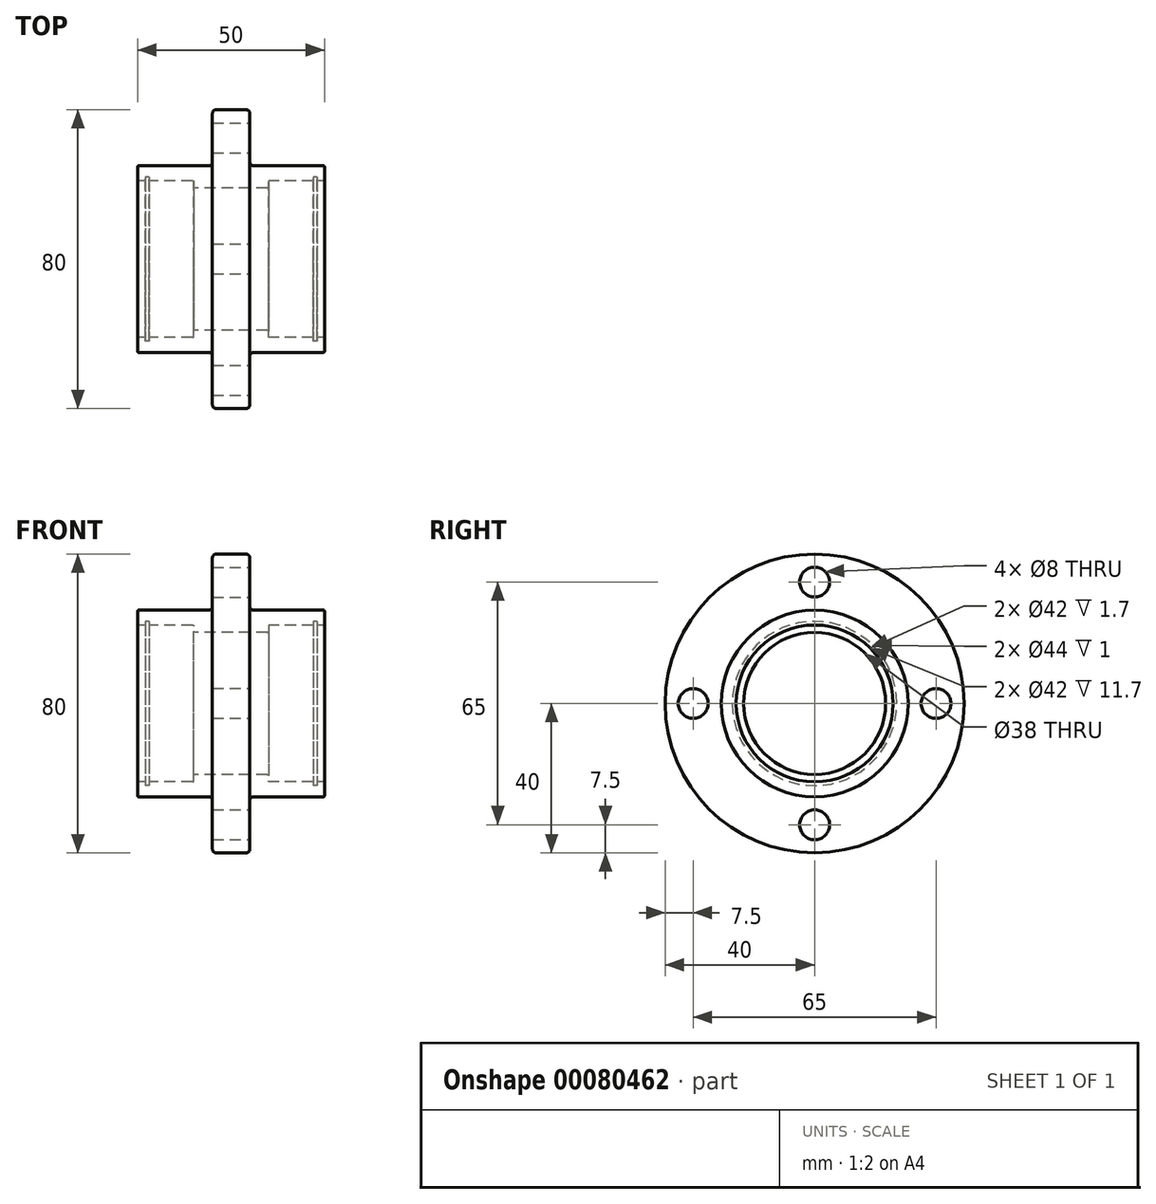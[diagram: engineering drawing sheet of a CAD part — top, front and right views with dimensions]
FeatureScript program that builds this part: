
annotation { "Feature Type Name" : "Feature", "Feature Type Description" : "" }
export const myFeature = defineFeature(function(context is Context, id is Id, definition is map)
    precondition{}
    {
        {
            var Q0;
            Q0=qCreatedBy(makeId("Front.planeOp"),FACE);
            var sketch = newSketch(context, id + "F0", { "sketchPlane" : qUnion([Q0])});
            skLineSegment(sketch, "E0", {"start": v(0, 0) * mm, "end": v(52.45, 0) * mm, "construction": true});
            skLineSegment(sketch, "E1", {"start": v(0, 21) * mm, "end": v(15, 21) * mm});
            skLineSegment(sketch, "E2", {"start": v(15, 21) * mm, "end": v(15, 19) * mm});
            skLineSegment(sketch, "E3", {"start": v(15, 19) * mm, "end": v(35, 19) * mm});
            skLineSegment(sketch, "E4", {"start": v(50, 21) * mm, "end": v(50, 25) * mm});
            skLineSegment(sketch, "E5", {"start": v(50, 25) * mm, "end": v(30, 25) * mm});
            skLineSegment(sketch, "E6", {"start": v(30, 25) * mm, "end": v(30, 40) * mm});
            skLineSegment(sketch, "E7", {"start": v(0, 25) * mm, "end": v(0, 21) * mm});
            skLineSegment(sketch, "E8.bottom", {"start": v(2, 21) * mm, "end": v(3, 21) * mm});
            skLineSegment(sketch, "E8.top", {"start": v(2, 22) * mm, "end": v(3, 22) * mm});
            skLineSegment(sketch, "E8.left", {"start": v(2, 21) * mm, "end": v(2, 22) * mm});
            skLineSegment(sketch, "E8.right", {"start": v(3, 21) * mm, "end": v(3, 22) * mm});
            skLineSegment(sketch, "E9", {"start": v(0, 25) * mm, "end": v(20, 25) * mm});
            skLineSegment(sketch, "E10", {"start": v(20, 25) * mm, "end": v(20, 40) * mm});
            skLineSegment(sketch, "E11", {"start": v(20, 40) * mm, "end": v(30, 40) * mm});
            skLineSegment(sketch, "E12", {"start": v(35, 19) * mm, "end": v(35, 21) * mm});
            skLineSegment(sketch, "E13", {"start": v(35, 21) * mm, "end": v(50, 21) * mm});
            skLineSegment(sketch, "E14.bottom", {"start": v(47, 21) * mm, "end": v(48, 21) * mm});
            skLineSegment(sketch, "E14.top", {"start": v(47, 22) * mm, "end": v(48, 22) * mm});
            skLineSegment(sketch, "E14.left", {"start": v(47, 21) * mm, "end": v(47, 22) * mm});
            skLineSegment(sketch, "E14.right", {"start": v(48, 21) * mm, "end": v(48, 22) * mm});
            skSolve(sketch);
        }
        {
            var Q0;
            {var subQ4=sQuery(id+"F0.wireOp",EDGE,"E2");Q0=makeQuery(id+"F0.imprint","IMPRINT",FACE,{"disambiguationData":[TD([[makeQuery(id+"F0.imprint","IMPRINT",EDGE,{"derivedFrom":subQ4}),1.0]])]});}
            var Q1;
            Q1=sQuery(id+"F0.wireOp",EDGE,"E0");
            revolve(context, id + "F1", {"entities" : qUnion([Q0]), "axis" : qUnion([Q1]), "revolveType" : RevolveType.FULL});
        }
        {
            var Q0;
            Q0=makeQuery(id+"F1.opRevolve","SWEPT_EDGE",EDGE,{"disambiguationData":[OSD([sQuery(id+"F0.wireOp",EDGE,"E1"),sQuery(id+"F0.wireOp",EDGE,"E2")])]});
            var Q1;
            Q1=makeQuery(id+"F1.opRevolve","SWEPT_EDGE",EDGE,{"disambiguationData":[OSD([sQuery(id+"F0.wireOp",EDGE,"E1"),sQuery(id+"F0.wireOp",EDGE,"E7")])]});
            var Q2;
            Q2=makeQuery(id+"F1.opRevolve","SWEPT_EDGE",EDGE,{"disambiguationData":[OSD([sQuery(id+"F0.wireOp",EDGE,"E2"),sQuery(id+"F0.wireOp",EDGE,"E3")])]});
            var Q3;
            Q3=makeQuery(id+"F1.opRevolve","SWEPT_EDGE",EDGE,{"disambiguationData":[OSD([sQuery(id+"F0.wireOp",EDGE,"E3"),sQuery(id+"F0.wireOp",EDGE,"E4")])]});
            var Q4;
            Q4=makeQuery(id+"F1.opRevolve","SWEPT_EDGE",EDGE,{"disambiguationData":[OSD([sQuery(id+"F0.wireOp",EDGE,"E12"),sQuery(id+"F0.wireOp",EDGE,"E13")])]});
            var Q5;
            Q5=makeQuery(id+"F1.opRevolve","SWEPT_EDGE",EDGE,{"disambiguationData":[OSD([sQuery(id+"F0.wireOp",EDGE,"E7"),sQuery(id+"F0.wireOp",EDGE,"E9")])]});
            fillet(context, id + "F2", {"entities" : qUnion([Q0, Q1, Q2, Q3, Q4, Q5]), "radius" : 0.3 * mm, "tangentPropagation" : true, "allowEdgeOverflow" : false});
        }
        {
            var Q0;
            Q0=makeQuery(id+"F1.opRevolve","SWEPT_EDGE",EDGE,{"disambiguationData":[OSD([sQuery(id+"F0.wireOp",EDGE,"E4"),sQuery(id+"F0.wireOp",EDGE,"E5")])]});
            var Q1;
            Q1=makeQuery(id+"F1.opRevolve","SWEPT_EDGE",EDGE,{"disambiguationData":[OSD([sQuery(id+"F0.wireOp",EDGE,"E5"),sQuery(id+"F0.wireOp",EDGE,"E6")])]});
            var Q2;
            Q2=makeQuery(id+"F1.opRevolve","SWEPT_EDGE",EDGE,{"disambiguationData":[OSD([sQuery(id+"F0.wireOp",EDGE,"E6"),sQuery(id+"F0.wireOp",EDGE,"8emcx9UW-5Iw0-E7Tb-gsbx-hsyMrdxOOZ0F")])]});
            var Q3;
            Q3=makeQuery(id+"F1.opRevolve","SWEPT_EDGE",EDGE,{"disambiguationData":[OSD([sQuery(id+"F0.wireOp",EDGE,"8emcx9UW-5Iw0-E7Tb-gsbx-hsyMrdxOOZ0F"),sQuery(id+"F0.wireOp",EDGE,"E7")])]});
            var Q4;
            Q4=makeQuery(id+"F1.opRevolve","SWEPT_EDGE",EDGE,{"disambiguationData":[OSD([sQuery(id+"F0.wireOp",EDGE,"E10"),sQuery(id+"F0.wireOp",EDGE,"E11")])]});
            var Q5;
            Q5=makeQuery(id+"F1.opRevolve","SWEPT_EDGE",EDGE,{"disambiguationData":[OSD([sQuery(id+"F0.wireOp",EDGE,"E9"),sQuery(id+"F0.wireOp",EDGE,"E10")])]});
            fillet(context, id + "F3", {"entities" : qUnion([Q0, Q1, Q2, Q3, Q4, Q5]), "radius" : 1 * mm, "tangentPropagation" : true, "allowEdgeOverflow" : false});
        }
        {
            var Q0;
            Q0=makeQuery(id+"F1.opRevolve","SWEPT_FACE",FACE,{"disambiguationData":[OSD([sQuery(id+"F0.wireOp",EDGE,"E6")])]});
            var sketch = newSketch(context, id + "F4", { "sketchPlane" : qUnion([Q0])});
            skCircle(sketch, "E15", {"center": v(0, 0) * mm, "radius": 32.5 * mm, "construction": true});
            skCircle(sketch, "E16", {"center": v(0, 32.5) * mm, "radius": 4 * mm});
            skCircle(sketch, "E17.1.0", {"center": v(-32.5, 0) * mm, "radius": 4 * mm});
            skCircle(sketch, "E17.2.0", {"center": v(0, -32.5) * mm, "radius": 4 * mm});
            skCircle(sketch, "E17.3.0", {"center": v(32.5, 0) * mm, "radius": 4 * mm});
            skSolve(sketch);
        }
        {
            var Q0;
            Q0 = qSketchRegion(id + "F4", true);
            extrude(context, id + "F5", {"entities" : qUnion([Q0]), "operationType" : NewBodyOperationType.REMOVE, "endBound" : BoundingType.THROUGH_ALL, "oppositeDirection" : true, "depth" : 25 * mm});
        }
    });
